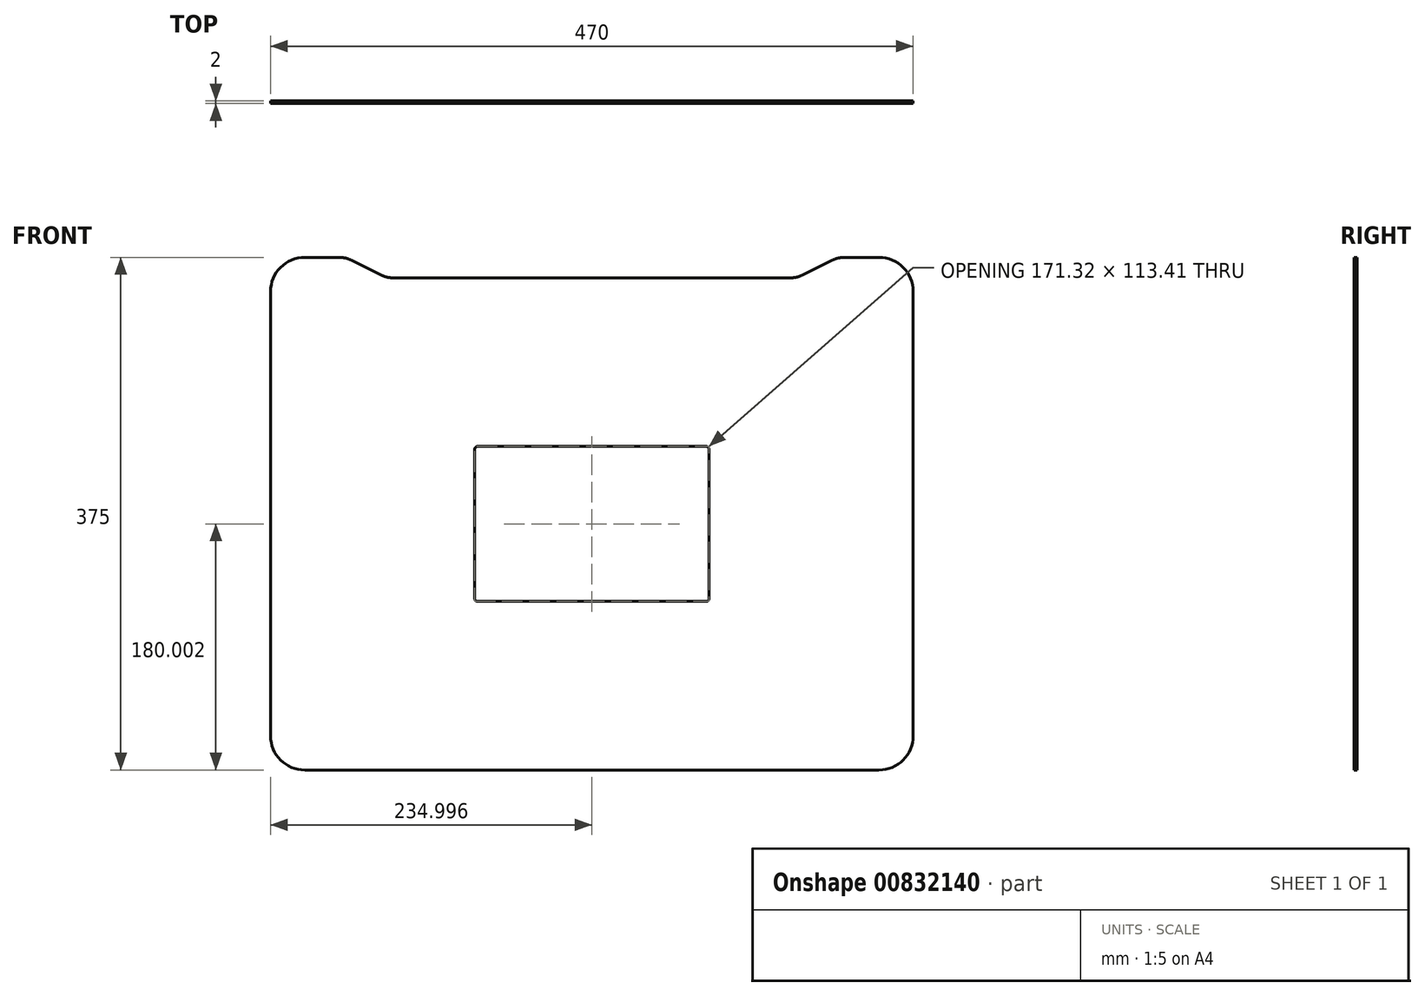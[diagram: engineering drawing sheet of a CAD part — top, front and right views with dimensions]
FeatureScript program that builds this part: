
annotation { "Feature Type Name" : "Feature", "Feature Type Description" : "" }
export const myFeature = defineFeature(function(context is Context, id is Id, definition is map)
    precondition{}
    {
        {
            var Q0;
            Q0=qCreatedBy(makeId("Front.planeOp"),FACE);
            var sketch = newSketch(context, id + "F0", { "sketchPlane" : qUnion([Q0])});
            skLineSegment(sketch, "E0.bottom", {"start": v(202.66, -149.74) * mm, "end": v(202.66, 175.26) * mm});
            skLineSegment(sketch, "E0.top", {"start": v(-267.34, -149.74) * mm, "end": v(-267.34, 175.26) * mm});
            skLineSegment(sketch, "E0.left", {"start": v(177.66, -174.74) * mm, "end": v(-242.34, -174.74) * mm});
            skPoint(sketch, "E0.middle", {"position": v(-32.34, 12.76) * mm});
            skLineSegment(sketch, "E1", {"start": v(-32.34, 185.26) * mm, "end": v(-182.34, 185.26) * mm});
            skLineSegment(sketch, "E2", {"start": v(-32.34, 185.26) * mm, "end": v(117.66, 185.26) * mm});
            skPoint(sketch, "E3.visualSharp", {"position": v(-267.34, 200.26) * mm});
            skArc(sketch, "E3.filletArc", {"start": v(-242.34, 200.26) * mm, "mid": v(-260.02, 192.94) * mm, "end": v(-267.34, 175.26) * mm});
            skPoint(sketch, "E4.visualSharp", {"position": v(202.66, 200.26) * mm});
            skArc(sketch, "E4.filletArc", {"start": v(202.66, 175.26) * mm, "mid": v(195.33, 192.94) * mm, "end": v(177.66, 200.26) * mm});
            skPoint(sketch, "E5.visualSharp", {"position": v(202.66, -174.74) * mm});
            skArc(sketch, "E5.filletArc", {"start": v(177.66, -174.74) * mm, "mid": v(195.33, -167.42) * mm, "end": v(202.66, -149.74) * mm});
            skPoint(sketch, "E6.visualSharp", {"position": v(-267.34, -174.74) * mm});
            skArc(sketch, "E6.filletArc", {"start": v(-267.34, -149.74) * mm, "mid": v(-260.02, -167.42) * mm, "end": v(-242.34, -174.74) * mm});
            skLineSegment(sketch, "E7", {"start": v(177.66, 200.26) * mm, "end": v(147.66, 200.26) * mm});
            skLineSegment(sketch, "E8", {"start": v(117.66, 185.26) * mm, "end": v(147.66, 200.26) * mm});
            skLineSegment(sketch, "E9", {"start": v(-242.34, 200.26) * mm, "end": v(-212.34, 200.26) * mm});
            skLineSegment(sketch, "E10", {"start": v(-212.34, 200.26) * mm, "end": v(-182.34, 185.26) * mm});
            skSolve(sketch);
        }
        {
            var Q0;
            Q0 = qSketchRegion(id + "F0", true);
            extrude(context, id + "F1", {"entities" : qUnion([Q0]), "depth" : 2 * mm, "offsetDistance" : 25.4 * mm});
        }
        {
            var Q0;
            Q0=makeQuery(id+"F1.opExtrude","CAP_FACE",FACE,{"disambiguationData":[OSD([sQuery(id+"F0.wireOp",EDGE,"E0.bottom"),sQuery(id+"F0.wireOp",EDGE,"E0.top"),sQuery(id+"F0.wireOp",EDGE,"E0.left"),sQuery(id+"F0.wireOp",EDGE,"E1"),sQuery(id+"F0.wireOp",EDGE,"E2"),sQuery(id+"F0.wireOp",EDGE,"E3.filletArc"),sQuery(id+"F0.wireOp",EDGE,"E4.filletArc"),sQuery(id+"F0.wireOp",EDGE,"E5.filletArc"),sQuery(id+"F0.wireOp",EDGE,"E6.filletArc"),sQuery(id+"F0.wireOp",EDGE,"E7"),sQuery(id+"F0.wireOp",EDGE,"E8"),sQuery(id+"F0.wireOp",EDGE,"E9"),sQuery(id+"F0.wireOp",EDGE,"E10")])],"isStart":false});
            var sketch = newSketch(context, id + "F2", { "sketchPlane" : qUnion([Q0])});
            skLineSegment(sketch, "E11.bottom", {"start": v(51.32, -51.44) * mm, "end": v(-116, -51.44) * mm});
            skLineSegment(sketch, "E11.top", {"start": v(51.32, 61.97) * mm, "end": v(-116, 61.97) * mm});
            skLineSegment(sketch, "E11.left", {"start": v(53.32, -49.44) * mm, "end": v(53.32, 59.97) * mm});
            skLineSegment(sketch, "E11.right", {"start": v(-118, -49.44) * mm, "end": v(-118, 59.97) * mm});
            skPoint(sketch, "E11.middle", {"position": v(-32.34, 5.26) * mm});
            skPoint(sketch, "E12.visualSharp", {"position": v(53.32, 61.97) * mm});
            skArc(sketch, "E12.filletArc", {"start": v(53.32, 59.97) * mm, "mid": v(52.73, 61.38) * mm, "end": v(51.32, 61.97) * mm});
            skPoint(sketch, "E13.visualSharp", {"position": v(53.32, -51.44) * mm});
            skArc(sketch, "E13.filletArc", {"start": v(51.32, -51.44) * mm, "mid": v(52.73, -50.86) * mm, "end": v(53.32, -49.44) * mm});
            skPoint(sketch, "E14.visualSharp", {"position": v(-118, -51.44) * mm});
            skArc(sketch, "E14.filletArc", {"start": v(-118, -49.44) * mm, "mid": v(-117.42, -50.86) * mm, "end": v(-116, -51.44) * mm});
            skPoint(sketch, "E15.visualSharp", {"position": v(-118, 61.97) * mm});
            skArc(sketch, "E15.filletArc", {"start": v(-116, 61.97) * mm, "mid": v(-117.42, 61.38) * mm, "end": v(-118, 59.97) * mm});
            skSolve(sketch);
        }
        {
            var Q0;
            Q0 = qSketchRegion(id + "F2", true);
            extrude(context, id + "F3", {"entities" : qUnion([Q0]), "operationType" : NewBodyOperationType.REMOVE, "oppositeDirection" : true, "depth" : 25.4 * mm, "offsetDistance" : 25.4 * mm});
        }
        {
            var Q0;
            Q0=makeQuery(id+"F1.opExtrude","SWEPT_EDGE",EDGE,{"disambiguationData":[OSD([sQuery(id+"F0.wireOp",EDGE,"E7"),sQuery(id+"F0.wireOp",EDGE,"E8")])]});
            var Q1;
            Q1=makeQuery(id+"F1.opExtrude","SWEPT_EDGE",EDGE,{"disambiguationData":[OSD([sQuery(id+"F0.wireOp",EDGE,"E2"),sQuery(id+"F0.wireOp",EDGE,"E8")])]});
            var Q2;
            Q2=makeQuery(id+"F1.opExtrude","SWEPT_EDGE",EDGE,{"disambiguationData":[OSD([sQuery(id+"F0.wireOp",EDGE,"E9"),sQuery(id+"F0.wireOp",EDGE,"E10")])]});
            var Q3;
            Q3=makeQuery(id+"F1.opExtrude","SWEPT_EDGE",EDGE,{"disambiguationData":[OSD([sQuery(id+"F0.wireOp",EDGE,"E1"),sQuery(id+"F0.wireOp",EDGE,"E10")])]});
            fillet(context, id + "F4", {"entities" : qUnion([Q0, Q1, Q2, Q3]), "radius" : 20 * mm, "tangentPropagation" : true, "allowEdgeOverflow" : false});
        }
    });
